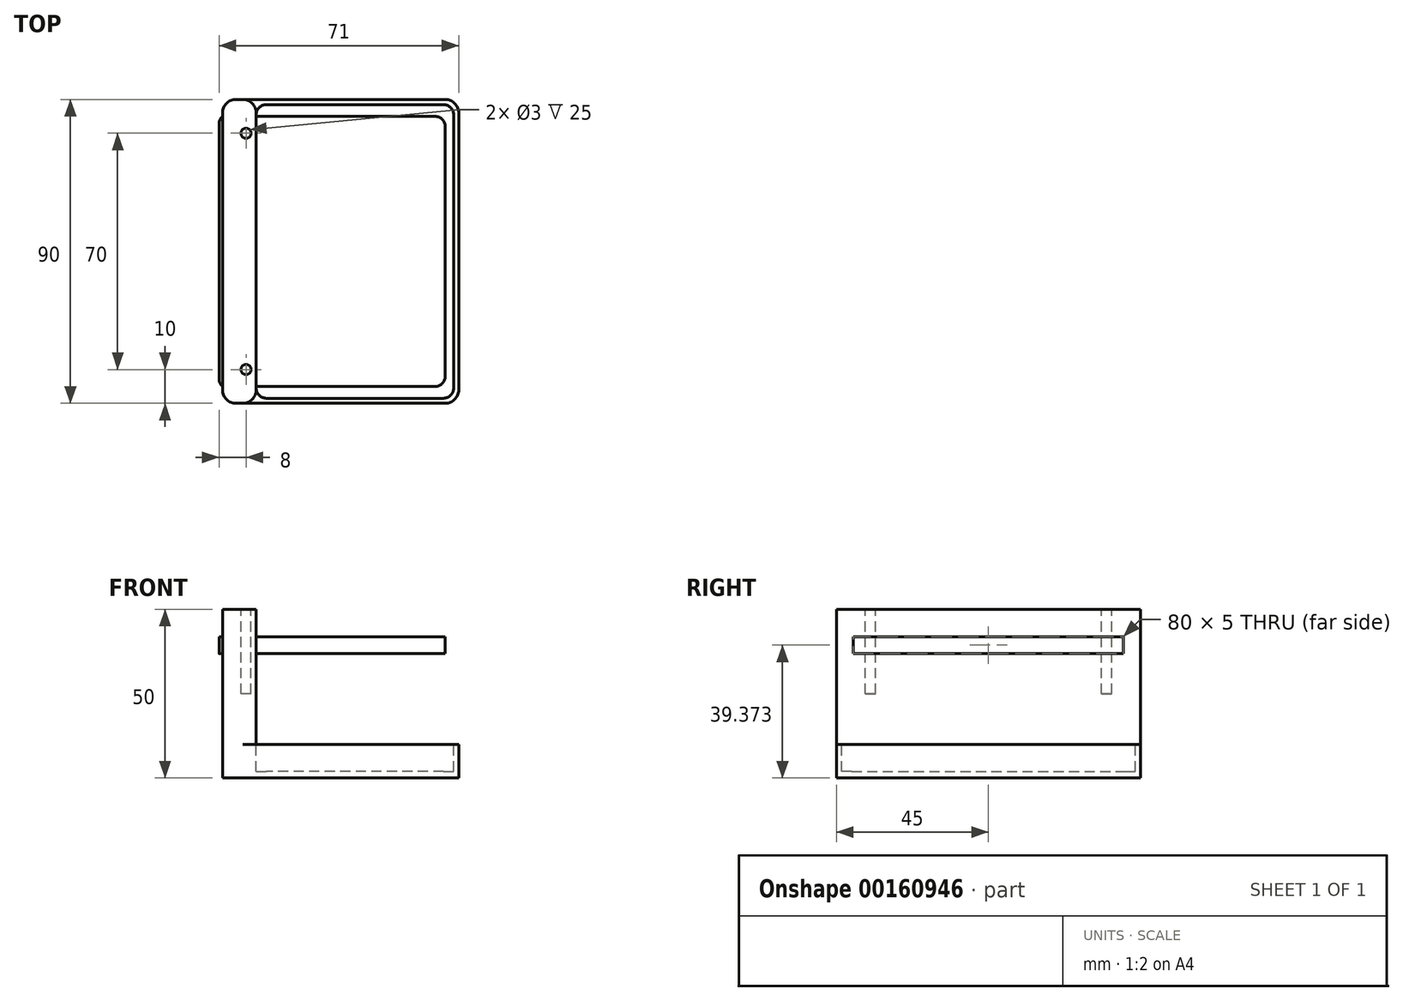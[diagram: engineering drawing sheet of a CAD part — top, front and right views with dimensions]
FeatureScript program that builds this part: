
annotation { "Feature Type Name" : "Feature", "Feature Type Description" : "" }
export const myFeature = defineFeature(function(context is Context, id is Id, definition is map)
    precondition{}
    {
        {
            var Q0;
            Q0=qCreatedBy(makeId("Front.planeOp"),FACE);
            var sketch = newSketch(context, id + "F0", { "sketchPlane" : qUnion([Q0])});
            skLineSegment(sketch, "E0", {"start": v(0, 0) * mm, "end": v(70, 0) * mm});
            skLineSegment(sketch, "E1", {"start": v(70, 0) * mm, "end": v(70, 10) * mm});
            skLineSegment(sketch, "E2", {"start": v(70, 10) * mm, "end": v(10, 10) * mm});
            skLineSegment(sketch, "E3", {"start": v(10, 10) * mm, "end": v(10, 50) * mm});
            skLineSegment(sketch, "E4", {"start": v(10, 50) * mm, "end": v(0, 50) * mm});
            skLineSegment(sketch, "E5", {"start": v(0, 50) * mm, "end": v(0, 0) * mm});
            skSolve(sketch);
        }
        {
            var Q0;
            Q0=makeQuery(id+"F0.imprint","IMPRINT",FACE,{"disambiguationData":[TD([[makeQuery(id+"F0.imprint","IMPRINT",EDGE,{"derivedFrom":sQuery(id+"F0.wireOp",EDGE,"E0")}),1.0]])]});
            extrude(context, id + "F1", {"entities" : qUnion([Q0]), "depth" : 45 * mm, "hasSecondDirection" : true, "secondDirectionOppositeDirection" : true, "secondDirectionDepth" : 45 * mm});
        }
        {
            var Q0;
            Q0=qCreatedBy(makeId("Front.planeOp"),FACE);
            var sketch = newSketch(context, id + "F2", { "sketchPlane" : qUnion([Q0])});
            skLineSegment(sketch, "E6.bottom", {"start": v(-1, 41.87) * mm, "end": v(66, 41.87) * mm});
            skLineSegment(sketch, "E6.top", {"start": v(-1, 36.87) * mm, "end": v(66, 36.87) * mm});
            skLineSegment(sketch, "E6.left", {"start": v(-1, 41.87) * mm, "end": v(-1, 36.87) * mm});
            skLineSegment(sketch, "E6.right", {"start": v(66, 41.87) * mm, "end": v(66, 36.87) * mm});
            skSolve(sketch);
        }
        {
            var Q0;
            Q0=qSketchRegion(id+"F2",true);
            extrude(context, id + "F3", {"entities" : qUnion([Q0]), "operationType" : NewBodyOperationType.ADD, "oppositeDirection" : true, "depth" : 40 * mm, "hasSecondDirection" : true, "secondDirectionOppositeDirection" : false, "secondDirectionDepth" : 40 * mm});
        }
        {
            var Q0;
            Q0=makeQuery(id+"F1.opExtrude","SWEPT_FACE",FACE,{"disambiguationData":[OSD([sQuery(id+"F0.wireOp",EDGE,"E4")])]});
            cPlane(context, id + "F4", {"entities" : qUnion([Q0]), "cplaneType" : CPlaneType.OFFSET, "offset" : 5 * mm, "width" : 150 * mm, "height" : 150 * mm});
        }
        {
            var Q0;
            Q0=qCreatedBy(id+"F4.planeOp",FACE);
            var sketch = newSketch(context, id + "F5", { "sketchPlane" : qUnion([Q0])});
            skCircle(sketch, "E7", {"center": v(7, -35) * mm, "radius": 1.5 * mm});
            skCircle(sketch, "E8", {"center": v(7, 35) * mm, "radius": 1.5 * mm});
            skSolve(sketch);
        }
        {
            var Q0;
            Q0=qSketchRegion(id+"F5",true);
            extrude(context, id + "F6", {"entities" : qUnion([Q0]), "operationType" : NewBodyOperationType.REMOVE, "oppositeDirection" : true, "depth" : 30 * mm});
        }
        {
            var Q0;
            Q0=makeQuery(id+"F1.opExtrude","SWEPT_FACE",FACE,{"disambiguationData":[OSD([sQuery(id+"F0.wireOp",EDGE,"E2")])]});
            var sketch = newSketch(context, id + "F7", { "sketchPlane" : qUnion([Q0])});
            skLineSegment(sketch, "E9.bottom", {"start": v(65.5, 43.5) * mm, "end": v(13, 43.5) * mm});
            skLineSegment(sketch, "E9.top", {"start": v(65.5, -43.5) * mm, "end": v(13, -43.5) * mm});
            skLineSegment(sketch, "E9.left", {"start": v(68.5, 40.5) * mm, "end": v(68.5, -40.5) * mm});
            skLineSegment(sketch, "E9.right", {"start": v(10, 40.5) * mm, "end": v(10, -40.5) * mm});
            skPoint(sketch, "E10.visualSharp", {"position": v(10, -43.5) * mm});
            skArc(sketch, "E10.filletArc", {"start": v(10, -40.5) * mm, "mid": v(10.88, -42.62) * mm, "end": v(13, -43.5) * mm});
            skPoint(sketch, "E11.visualSharp", {"position": v(10, 43.5) * mm});
            skArc(sketch, "E11.filletArc", {"start": v(13, 43.5) * mm, "mid": v(10.88, 42.62) * mm, "end": v(10, 40.5) * mm});
            skPoint(sketch, "E12.visualSharp", {"position": v(68.5, -43.5) * mm});
            skArc(sketch, "E12.filletArc", {"start": v(65.5, -43.5) * mm, "mid": v(67.62, -42.62) * mm, "end": v(68.5, -40.5) * mm});
            skPoint(sketch, "E13.visualSharp", {"position": v(68.5, 43.5) * mm});
            skArc(sketch, "E13.filletArc", {"start": v(68.5, 40.5) * mm, "mid": v(67.62, 42.62) * mm, "end": v(65.5, 43.5) * mm});
            skSolve(sketch);
        }
        {
            var Q0;
            Q0=makeQuery(id+"F7.imprint","IMPRINT",FACE,{"disambiguationData":[TD([[makeQuery(id+"F7.imprint","IMPRINT",EDGE,{"derivedFrom":sQuery(id+"F7.wireOp",EDGE,"E9.bottom")}),1.0]])]});
            extrude(context, id + "F8", {"entities" : qUnion([Q0]), "operationType" : NewBodyOperationType.REMOVE, "oppositeDirection" : true, "depth" : 8 * mm});
        }
        {
            var Q0;
            Q0=makeQuery(id+"F1.opExtrude","CAP_EDGE",EDGE,{"disambiguationData":[OSD([sQuery(id+"F0.wireOp",EDGE,"E1")])],"isStart":false});
            var Q1;
            Q1=makeQuery(id+"F1.opExtrude","CAP_EDGE",EDGE,{"disambiguationData":[OSD([sQuery(id+"F0.wireOp",EDGE,"E1")])],"isStart":true});
            var Q2;
            Q2=makeQuery(id+"F1.opExtrude","CAP_EDGE",EDGE,{"disambiguationData":[OSD([sQuery(id+"F0.wireOp",EDGE,"E5")])],"isStart":false});
            var Q3;
            Q3=makeQuery(id+"F1.opExtrude","CAP_EDGE",EDGE,{"disambiguationData":[OSD([sQuery(id+"F0.wireOp",EDGE,"E5")])],"isStart":true});
            var Q4;
            Q4=makeQuery(id+"F1.opExtrude","CAP_EDGE",EDGE,{"disambiguationData":[OSD([sQuery(id+"F0.wireOp",EDGE,"E3")])],"isStart":false});
            var Q5;
            Q5=makeQuery(id+"F1.opExtrude","CAP_EDGE",EDGE,{"disambiguationData":[OSD([sQuery(id+"F0.wireOp",EDGE,"E3")])],"isStart":true});
            fillet(context, id + "F9", {"entities" : qUnion([Q0, Q1, Q2, Q3, Q4, Q5]), "radius" : 4 * mm, "tangentPropagation" : true, "allowEdgeOverflow" : false});
        }
        {
            var Q0;
            Q0=makeQuery(id+"F3.opExtrude","CAP_EDGE",EDGE,{"disambiguationData":[OSD([sQuery(id+"F2.wireOp",EDGE,"E6.right")])],"isStart":true});
            var Q1;
            Q1=makeQuery(id+"F3.opExtrude","CAP_EDGE",EDGE,{"disambiguationData":[OSD([sQuery(id+"F2.wireOp",EDGE,"E6.right")])],"isStart":false});
            var Q2;
            Q2=makeQuery(id+"F3.opExtrude","CAP_EDGE",EDGE,{"disambiguationData":[OSD([sQuery(id+"F2.wireOp",EDGE,"E6.left")])],"isStart":false});
            var Q3;
            Q3=makeQuery(id+"F3.opExtrude","CAP_EDGE",EDGE,{"disambiguationData":[OSD([sQuery(id+"F2.wireOp",EDGE,"E6.left")])],"isStart":true});
            fillet(context, id + "F10", {"entities" : qUnion([Q0, Q1, Q2, Q3]), "radius" : 3 * mm, "tangentPropagation" : true, "allowEdgeOverflow" : false});
        }
    });
